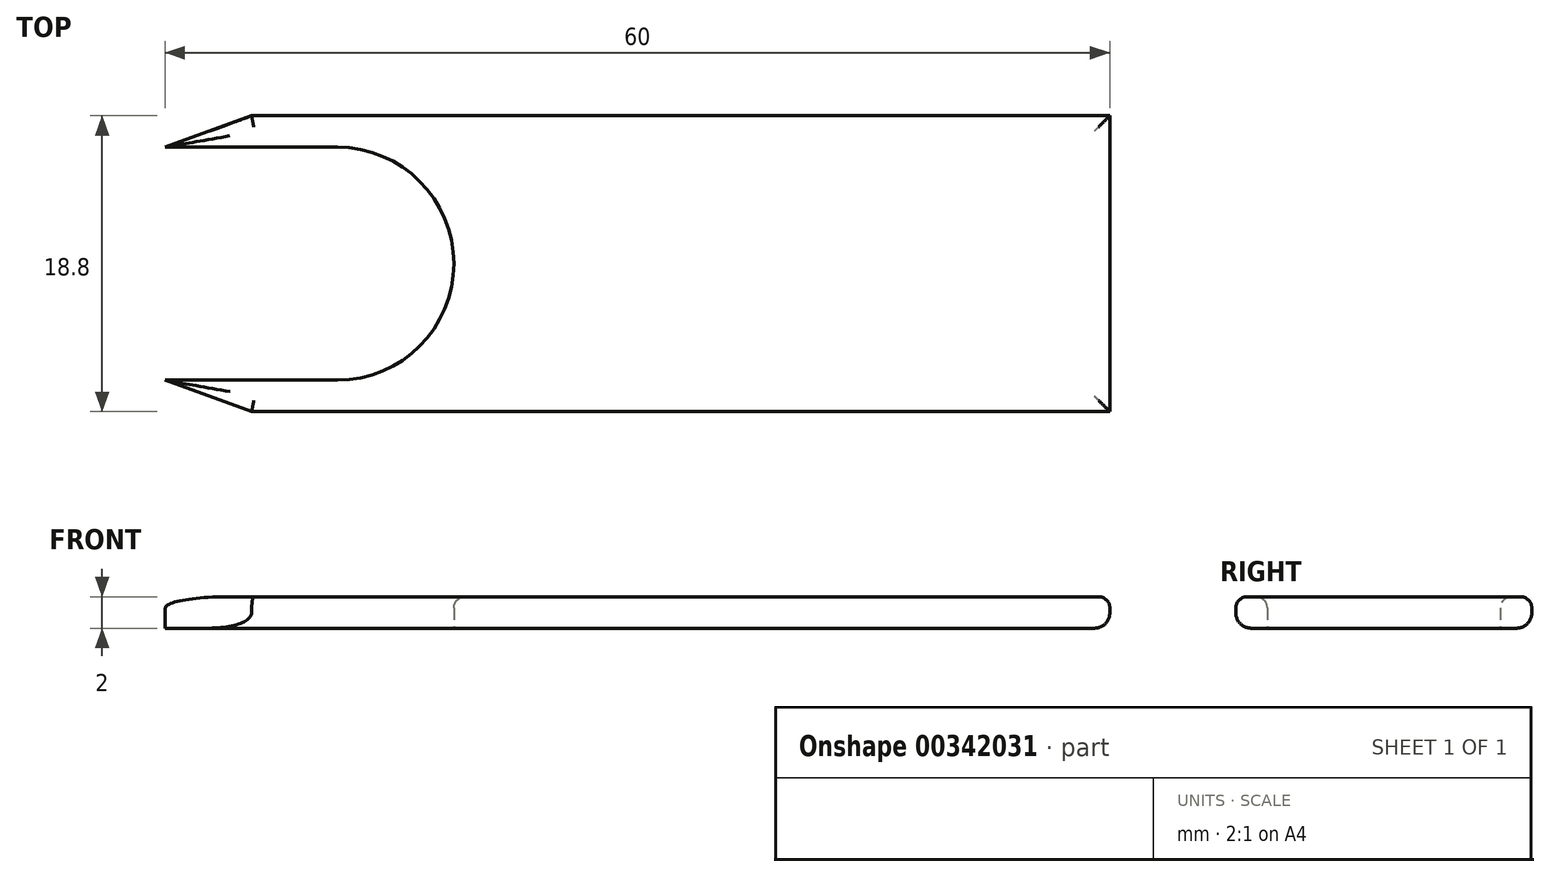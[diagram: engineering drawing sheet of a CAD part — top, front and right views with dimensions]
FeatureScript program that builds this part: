
annotation { "Feature Type Name" : "Feature", "Feature Type Description" : "" }
export const myFeature = defineFeature(function(context is Context, id is Id, definition is map)
    precondition{}
    {
        {
            var Q0;
            Q0=qCreatedBy(makeId("Top.planeOp"),FACE);
            var sketch = newSketch(context, id + "F0", { "sketchPlane" : qUnion([Q0])});
            skLineSegment(sketch, "E0.bottom", {"start": v(-30, 9.4) * mm, "end": v(30, 9.4) * mm});
            skLineSegment(sketch, "E0.top", {"start": v(-30, -9.4) * mm, "end": v(30, -9.4) * mm});
            skLineSegment(sketch, "E0.left", {"start": v(-30, 9.4) * mm, "end": v(-30, -9.4) * mm});
            skLineSegment(sketch, "E0.right", {"start": v(30, 9.4) * mm, "end": v(30, -9.4) * mm});
            skPoint(sketch, "E0.middle", {"position": v(0, 0) * mm});
            skSolve(sketch);
        }
        {
            var Q0;
            Q0=qCreatedBy(makeId("Top.planeOp"),FACE);
            var sketch = newSketch(context, id + "F1", { "sketchPlane" : qUnion([Q0])});
            skCircle(sketch, "E1", {"center": v(-19.06, 0) * mm, "radius": 7.4 * mm});
            skLineSegment(sketch, "E2.bottom", {"start": v(-59, 7.4) * mm, "end": v(-19.06, 7.4) * mm});
            skLineSegment(sketch, "E2.top", {"start": v(-59, -7.4) * mm, "end": v(-19.06, -7.4) * mm});
            skLineSegment(sketch, "E2.left", {"start": v(-59, 7.4) * mm, "end": v(-59, -7.4) * mm});
            skLineSegment(sketch, "E2.right", {"start": v(-19.06, 7.4) * mm, "end": v(-19.06, -7.4) * mm});
            skSolve(sketch);
        }
        {
            var Q0;
            Q0 = qSketchRegion(id + "F0", true);
            extrude(context, id + "F2", {"entities" : qUnion([Q0]), "depth" : 2 * mm});
        }
        {
            var Q0;
            Q0 = qSketchRegion(id + "F1", true);
            extrude(context, id + "F3", {"entities" : qUnion([Q0]), "depth" : 3 * mm});
        }
        {
            var Q0;
            Q0=makeQuery(id+"F3.opExtrude","SWEPT_BODY",BODY,{"disambiguationData":[OSD([sQuery(id+"F1.wireOp",EDGE,"E1"),sQuery(id+"F1.wireOp",EDGE,"E2.bottom"),sQuery(id+"F1.wireOp",EDGE,"E2.top"),sQuery(id+"F1.wireOp",EDGE,"E2.left")])]});
            var Q1;
            Q1=makeQuery(id+"F2.opExtrude","SWEPT_BODY",BODY,{"disambiguationData":[OSD([sQuery(id+"F0.wireOp",EDGE,"E0.bottom"),sQuery(id+"F0.wireOp",EDGE,"E0.top"),sQuery(id+"F0.wireOp",EDGE,"E0.left"),sQuery(id+"F0.wireOp",EDGE,"E0.right")])]});
            booleanBodies(context, id + "F4", {"operationType" : BooleanOperationType.SUBTRACTION, "tools" : qUnion([Q0]), "targets" : qUnion([Q1])});
        }
        {
            var Q0;
            Q0=makeQuery(id+"F2.opExtrude","SWEPT_EDGE",EDGE,{"disambiguationData":[OSD([sQuery(id+"F0.wireOp",EDGE,"E0.top"),sQuery(id+"F0.wireOp",EDGE,"E0.left")])]});
            chamfer(context, id + "F5", {"entities" : qUnion([Q0]), "chamferType" : ChamferType.OFFSET_ANGLE, "width" : 5.5 * mm, "oppositeDirection" : false, "angle" : 20 * degree, "tangentPropagation" : true});
        }
        {
            var Q0;
            Q0=makeQuery(id+"F2.opExtrude","SWEPT_EDGE",EDGE,{"disambiguationData":[OSD([sQuery(id+"F0.wireOp",EDGE,"E0.bottom"),sQuery(id+"F0.wireOp",EDGE,"E0.left")])]});
            chamfer(context, id + "F6", {"entities" : qUnion([Q0]), "chamferType" : ChamferType.OFFSET_ANGLE, "width" : 2 * mm, "oppositeDirection" : false, "angle" : 70 * degree, "tangentPropagation" : true});
        }
        {
            var Q0;
            Q0=makeQuery(id+"F2.opExtrude","CAP_EDGE",EDGE,{"disambiguationData":[OSD([sQuery(id+"F0.wireOp",EDGE,"E0.top")])],"isStart":false});
            var Q1;
            Q1=makeQuery(id+"F2.opExtrude","CAP_EDGE",EDGE,{"disambiguationData":[OSD([sQuery(id+"F0.wireOp",EDGE,"E0.bottom")])],"isStart":false});
            var Q2;
            Q2=makeQuery(id+"F2.opExtrude","CAP_EDGE",EDGE,{"disambiguationData":[OSD([sQuery(id+"F0.wireOp",EDGE,"E0.right")])],"isStart":false});
            var Q3;
            Q3=makeQuery(id+"F4.opBoolean","INTERSECT",EDGE,{"derivedFrom":[makeQuery(id+"F2.opExtrude","CAP_FACE",FACE,{"disambiguationData":[OSD([sQuery(id+"F0.wireOp",EDGE,"E0.bottom"),sQuery(id+"F0.wireOp",EDGE,"E0.top"),sQuery(id+"F0.wireOp",EDGE,"E0.left"),sQuery(id+"F0.wireOp",EDGE,"E0.right")])],"isStart":false}),makeQuery(id+"F3.opExtrude","SWEPT_FACE",FACE,{"disambiguationData":[OSD([sQuery(id+"F1.wireOp",EDGE,"E1")])]})]});
            var Q4;
            {var subQ0=sQuery(id+"F0.wireOp",EDGE,"E0.left");var subQ1=sQuery(id+"F0.wireOp",EDGE,"E0.top");Q4=makeQuery(id+"F5.opChamfer","BLEND_EDGE",EDGE,{"blendedFrom":[makeQuery(id+"F2.opExtrude","SWEPT_EDGE",EDGE,{"disambiguationData":[OSD([subQ1,subQ0])]}),makeQuery(id+"F2.opExtrude","CAP_FACE",FACE,{"disambiguationData":[OSD([sQuery(id+"F0.wireOp",EDGE,"E0.bottom"),subQ1,subQ0,sQuery(id+"F0.wireOp",EDGE,"E0.right")])],"isStart":false})],"blendedInto":[makeQuery(id+"F2.opExtrude","CAP_FACE",FACE,{"disambiguationData":[OSD([sQuery(id+"F0.wireOp",EDGE,"E0.bottom"),subQ1,subQ0,sQuery(id+"F0.wireOp",EDGE,"E0.right")])],"isStart":false})]});}
            var Q5;
            Q5=makeQuery(id+"F4.opBoolean","INTERSECT",EDGE,{"derivedFrom":[makeQuery(id+"F2.opExtrude","CAP_FACE",FACE,{"disambiguationData":[OSD([sQuery(id+"F0.wireOp",EDGE,"E0.bottom"),sQuery(id+"F0.wireOp",EDGE,"E0.top"),sQuery(id+"F0.wireOp",EDGE,"E0.left"),sQuery(id+"F0.wireOp",EDGE,"E0.right")])],"isStart":false}),makeQuery(id+"F3.opExtrude","SWEPT_FACE",FACE,{"disambiguationData":[OSD([sQuery(id+"F1.wireOp",EDGE,"E2.bottom")])]})]});
            var Q6;
            {var subQ0=sQuery(id+"F0.wireOp",EDGE,"E0.left");var subQ1=sQuery(id+"F0.wireOp",EDGE,"E0.bottom");Q6=makeQuery(id+"F6.opChamfer","BLEND_EDGE",EDGE,{"blendedFrom":[makeQuery(id+"F2.opExtrude","SWEPT_EDGE",EDGE,{"disambiguationData":[OSD([subQ1,subQ0])]}),makeQuery(id+"F2.opExtrude","CAP_FACE",FACE,{"disambiguationData":[OSD([subQ1,sQuery(id+"F0.wireOp",EDGE,"E0.top"),subQ0,sQuery(id+"F0.wireOp",EDGE,"E0.right")])],"isStart":false})],"blendedInto":[makeQuery(id+"F2.opExtrude","CAP_FACE",FACE,{"disambiguationData":[OSD([subQ1,sQuery(id+"F0.wireOp",EDGE,"E0.top"),subQ0,sQuery(id+"F0.wireOp",EDGE,"E0.right")])],"isStart":false})]});}
            var Q7;
            Q7=makeQuery(id+"F4.opBoolean","INTERSECT",EDGE,{"derivedFrom":[makeQuery(id+"F2.opExtrude","CAP_FACE",FACE,{"disambiguationData":[OSD([sQuery(id+"F0.wireOp",EDGE,"E0.bottom"),sQuery(id+"F0.wireOp",EDGE,"E0.top"),sQuery(id+"F0.wireOp",EDGE,"E0.left"),sQuery(id+"F0.wireOp",EDGE,"E0.right")])],"isStart":false}),makeQuery(id+"F3.opExtrude","SWEPT_FACE",FACE,{"disambiguationData":[OSD([sQuery(id+"F1.wireOp",EDGE,"E2.top")])]})]});
            fillet(context, id + "F7", {"entities" : qUnion([Q0, Q1, Q2, Q3, Q4, Q5, Q6, Q7]), "radius" : 0.72 * mm, "tangentPropagation" : true, "allowEdgeOverflow" : false});
        }
        {
            var Q0;
            Q0=makeQuery(id+"F2.opExtrude","CAP_EDGE",EDGE,{"disambiguationData":[OSD([sQuery(id+"F0.wireOp",EDGE,"E0.top")])],"isStart":true});
            var Q1;
            Q1=makeQuery(id+"F2.opExtrude","CAP_EDGE",EDGE,{"disambiguationData":[OSD([sQuery(id+"F0.wireOp",EDGE,"E0.right")])],"isStart":true});
            var Q2;
            Q2=makeQuery(id+"F2.opExtrude","CAP_EDGE",EDGE,{"disambiguationData":[OSD([sQuery(id+"F0.wireOp",EDGE,"E0.bottom")])],"isStart":true});
            fillet(context, id + "F8", {"entities" : qUnion([Q0, Q1, Q2]), "radius" : 0.97 * mm, "tangentPropagation" : true, "allowEdgeOverflow" : false});
        }
    });
